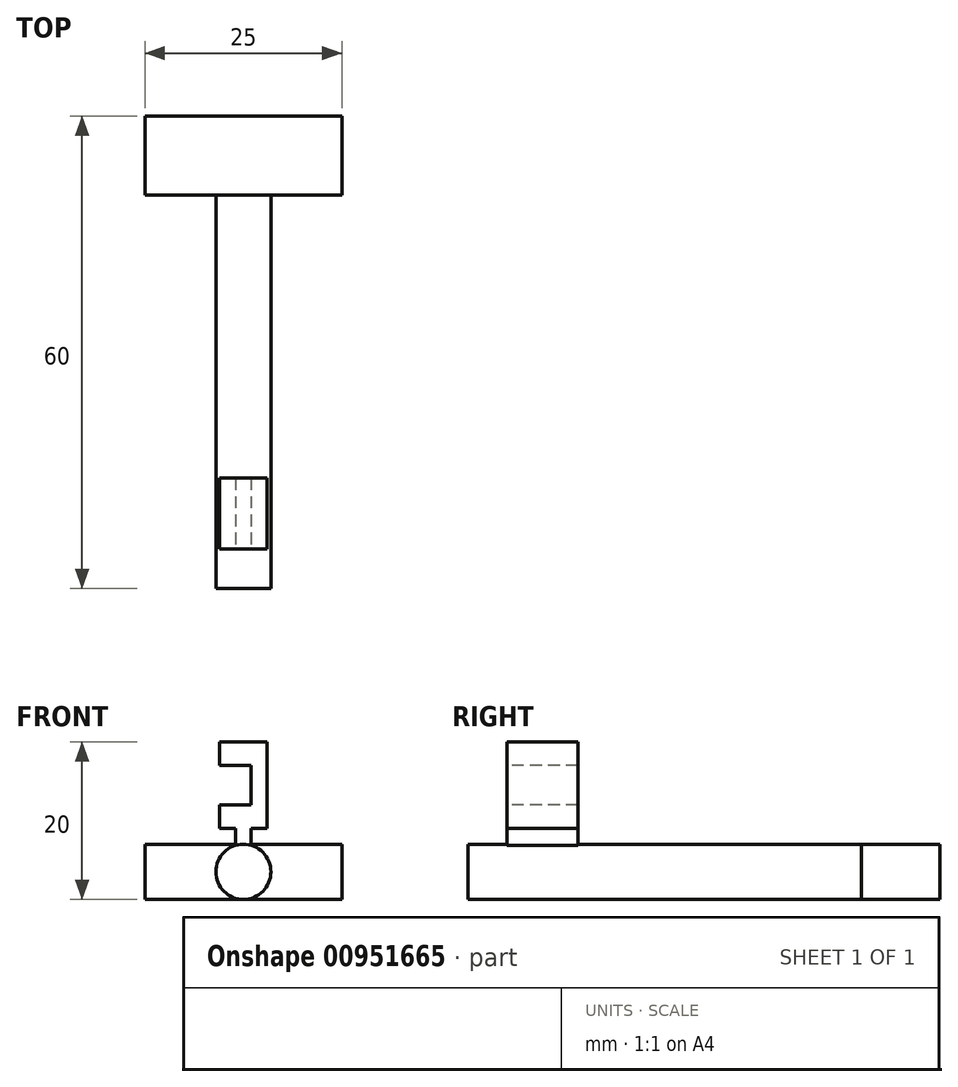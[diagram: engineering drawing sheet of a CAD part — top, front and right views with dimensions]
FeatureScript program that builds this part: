
annotation { "Feature Type Name" : "Feature", "Feature Type Description" : "" }
export const myFeature = defineFeature(function(context is Context, id is Id, definition is map)
    precondition{}
    {
        {
            var Q0;
            Q0=qCreatedBy(makeId("Front.planeOp"),FACE);
            var sketch = newSketch(context, id + "F0", { "sketchPlane" : qUnion([Q0])});
            skCircle(sketch, "E0", {"center": v(0.03, 3.5) * mm, "radius": 3.5 * mm});
            skPoint(sketch, "E0.first.point", {"position": v(0, 0) * mm});
            skPoint(sketch, "E0.second.point", {"position": v(0, 7) * mm});
            skPoint(sketch, "E0.third.point", {"position": v(3.49, 4.01) * mm});
            skLineSegment(sketch, "E1.bottom", {"start": v(1, 9) * mm, "end": v(-1, 9) * mm});
            skLineSegment(sketch, "E1.top", {"start": v(1, 5) * mm, "end": v(-1, 5) * mm});
            skLineSegment(sketch, "E1.left", {"start": v(1, 9) * mm, "end": v(1, 5) * mm});
            skLineSegment(sketch, "E1.right", {"start": v(-1, 9) * mm, "end": v(-1, 5) * mm});
            skLineSegment(sketch, "E2", {"start": v(0, 7) * mm, "end": v(0, 9) * mm});
            skLineSegment(sketch, "E3", {"start": v(0, 9) * mm, "end": v(-3, 9) * mm});
            skLineSegment(sketch, "E4.MirrorCS", {"start": v(0, 9) * mm, "end": v(3, 9) * mm});
            skLineSegment(sketch, "E5.bottom", {"start": v(-3, 9) * mm, "end": v(3, 9) * mm});
            skLineSegment(sketch, "E5.top", {"start": v(-3, 12) * mm, "end": v(3, 12) * mm});
            skLineSegment(sketch, "E5.left", {"start": v(-3, 9) * mm, "end": v(-3, 12) * mm});
            skLineSegment(sketch, "E5.right", {"start": v(3, 9) * mm, "end": v(3, 12) * mm});
            skLineSegment(sketch, "E6.bottom", {"start": v(1, 12) * mm, "end": v(3, 12) * mm});
            skLineSegment(sketch, "E6.top", {"start": v(1, 17) * mm, "end": v(3, 17) * mm});
            skLineSegment(sketch, "E6.left", {"start": v(1, 12) * mm, "end": v(1, 17) * mm});
            skLineSegment(sketch, "E6.right", {"start": v(3, 12) * mm, "end": v(3, 17) * mm});
            skLineSegment(sketch, "E7.bottom", {"start": v(3, 17) * mm, "end": v(-3, 17) * mm});
            skLineSegment(sketch, "E7.top", {"start": v(3, 20) * mm, "end": v(-3, 20) * mm});
            skLineSegment(sketch, "E7.left", {"start": v(3, 17) * mm, "end": v(3, 20) * mm});
            skLineSegment(sketch, "E7.right", {"start": v(-3, 17) * mm, "end": v(-3, 20) * mm});
            skSolve(sketch);
        }
        {
            var Q0;
            {var subQ5=sQuery(id+"F0.wireOp",EDGE,"E1.top");Q0=makeQuery(id+"F0.imprint","IMPRINT",FACE,{"disambiguationData":[TD([[makeQuery(id+"F0.imprint","IMPRINT",EDGE,{"derivedFrom":subQ5}),1.0]])]});}
            var Q1;
            {var subQ1=sQuery(id+"F0.wireOp",EDGE,"E1.top");Q1=makeQuery(id+"F0.imprint","IMPRINT",FACE,{"disambiguationData":[TD([[makeQuery(id+"F0.imprint","IMPRINT",EDGE,{"derivedFrom":subQ1}),-1.0]])]});}
            var Q2;
            {var subQ0=sQuery(id+"F0.wireOp",EDGE,"E2");Q2=makeQuery(id+"F0.imprint","IMPRINT",FACE,{"disambiguationData":[TD([[makeQuery(id+"F0.imprint","IMPRINT",EDGE,{"derivedFrom":subQ0}),1.0]])]});}
            var Q3;
            {var subQ0=sQuery(id+"F0.wireOp",EDGE,"E2");Q3=makeQuery(id+"F0.imprint","IMPRINT",FACE,{"disambiguationData":[TD([[makeQuery(id+"F0.imprint","IMPRINT",EDGE,{"derivedFrom":subQ0}),-1.0]])]});}
            var Q4;
            {var subQ1=sQuery(id+"F0.wireOp",EDGE,"E3");Q4=makeQuery(id+"F0.imprint","IMPRINT",FACE,{"disambiguationData":[TD([[makeQuery(id+"F0.imprint","IMPRINT",EDGE,{"derivedFrom":subQ1}),-1.0]])]});}
            var Q5;
            Q5=makeQuery(id+"F0.imprint","IMPRINT",FACE,{"disambiguationData":[TD([[makeQuery(id+"F0.imprint","IMPRINT",EDGE,{"derivedFrom":sQuery(id+"F0.wireOp",EDGE,"E6.top")}),-1.0]])]});
            var Q6;
            Q6=makeQuery(id+"F0.imprint","IMPRINT",FACE,{"disambiguationData":[TD([[makeQuery(id+"F0.imprint","IMPRINT",EDGE,{"derivedFrom":sQuery(id+"F0.wireOp",EDGE,"E6.top")}),1.0]])]});
            extrude(context, id + "F1", {"entities" : qUnion([Q0, Q1, Q2, Q3, Q4, Q5, Q6]), "oppositeDirection" : true, "depth" : 9 * mm, "offsetDistance" : 25 * mm});
        }
        {
            var Q0;
            {var subQ5=sQuery(id+"F0.wireOp",EDGE,"E1.top");Q0=makeQuery(id+"F0.imprint","IMPRINT",FACE,{"disambiguationData":[TD([[makeQuery(id+"F0.imprint","IMPRINT",EDGE,{"derivedFrom":subQ5}),1.0]])]});}
            var Q1;
            {var subQ1=sQuery(id+"F0.wireOp",EDGE,"E1.top");Q1=makeQuery(id+"F0.imprint","IMPRINT",FACE,{"disambiguationData":[TD([[makeQuery(id+"F0.imprint","IMPRINT",EDGE,{"derivedFrom":subQ1}),-1.0]])]});}
            extrude(context, id + "F2", {"entities" : qUnion([Q0, Q1]), "operationType" : NewBodyOperationType.ADD, "depth" : 5 * mm, "offsetDistance" : 25 * mm});
        }
        {
            var Q0;
            {var subQ5=sQuery(id+"F0.wireOp",EDGE,"E1.top");Q0=makeQuery(id+"F0.imprint","IMPRINT",FACE,{"disambiguationData":[TD([[makeQuery(id+"F0.imprint","IMPRINT",EDGE,{"derivedFrom":subQ5}),1.0]])]});}
            var Q1;
            {var subQ1=sQuery(id+"F0.wireOp",EDGE,"E1.top");Q1=makeQuery(id+"F0.imprint","IMPRINT",FACE,{"disambiguationData":[TD([[makeQuery(id+"F0.imprint","IMPRINT",EDGE,{"derivedFrom":subQ1}),-1.0]])]});}
            extrude(context, id + "F3", {"entities" : qUnion([Q0, Q1]), "operationType" : NewBodyOperationType.ADD, "oppositeDirection" : true, "depth" : 45 * mm, "offsetDistance" : 25 * mm});
        }
        {
            var Q0;
            Q0=makeQuery(id+"F3.opExtrude","CAP_FACE",FACE,{"disambiguationData":[OSD([sQuery(id+"F0.wireOp",EDGE,"E0")])],"isStart":false});
            var sketch = newSketch(context, id + "F4", { "sketchPlane" : qUnion([Q0])});
            skLineSegment(sketch, "E8.bottom", {"start": v(12.47, 0) * mm, "end": v(-12.53, 0) * mm});
            skLineSegment(sketch, "E8.top", {"start": v(12.47, 7) * mm, "end": v(-12.53, 7) * mm});
            skLineSegment(sketch, "E8.left", {"start": v(12.47, 0) * mm, "end": v(12.47, 7) * mm});
            skLineSegment(sketch, "E8.right", {"start": v(-12.53, 0) * mm, "end": v(-12.53, 7) * mm});
            skPoint(sketch, "E8.middle", {"position": v(-0.03, 3.5) * mm});
            skSolve(sketch);
        }
        {
            var Q0;
            {var subQ0=sQuery(id+"F4.wireOp",EDGE,"E8.left");Q0=makeQuery(id+"F4.imprint","IMPRINT",FACE,{"disambiguationData":[TD([[makeQuery(id+"F4.imprint","IMPRINT",EDGE,{"derivedFrom":subQ0}),1.0]])]});}
            var Q1;
            {var subQ0=sQuery(id+"F4.wireOp",EDGE,"E8.bottom");var subQ1=makeQuery(id+"F3.opExtrude","CAP_EDGE",EDGE,{"disambiguationData":[OSD([sQuery(id+"F0.wireOp",EDGE,"E0")])],"isStart":false});var subQ2=makeQuery(id+"F4.imprint","INTERSECT",VERTEX,{"disambiguationData":[OD(0.0)],"derivedFrom":[subQ1,subQ0]});Q1=makeQuery(id+"F4.imprint","IMPRINT",FACE,{"disambiguationData":[TD([[makeQuery(id+"F4.imprint","IMPRINT",EDGE,{"disambiguationData":[TD([[subQ2,1.0]])],"derivedFrom":subQ0}),-1.0]])]});}
            var Q2;
            {var subQ3=sQuery(id+"F4.wireOp",EDGE,"E8.right");Q2=makeQuery(id+"F4.imprint","IMPRINT",FACE,{"disambiguationData":[TD([[makeQuery(id+"F4.imprint","IMPRINT",EDGE,{"derivedFrom":subQ3}),-1.0]])]});}
            extrude(context, id + "F5", {"entities" : qUnion([Q0, Q1, Q2]), "operationType" : NewBodyOperationType.ADD, "depth" : 10 * mm, "offsetDistance" : 25 * mm});
        }
    });
